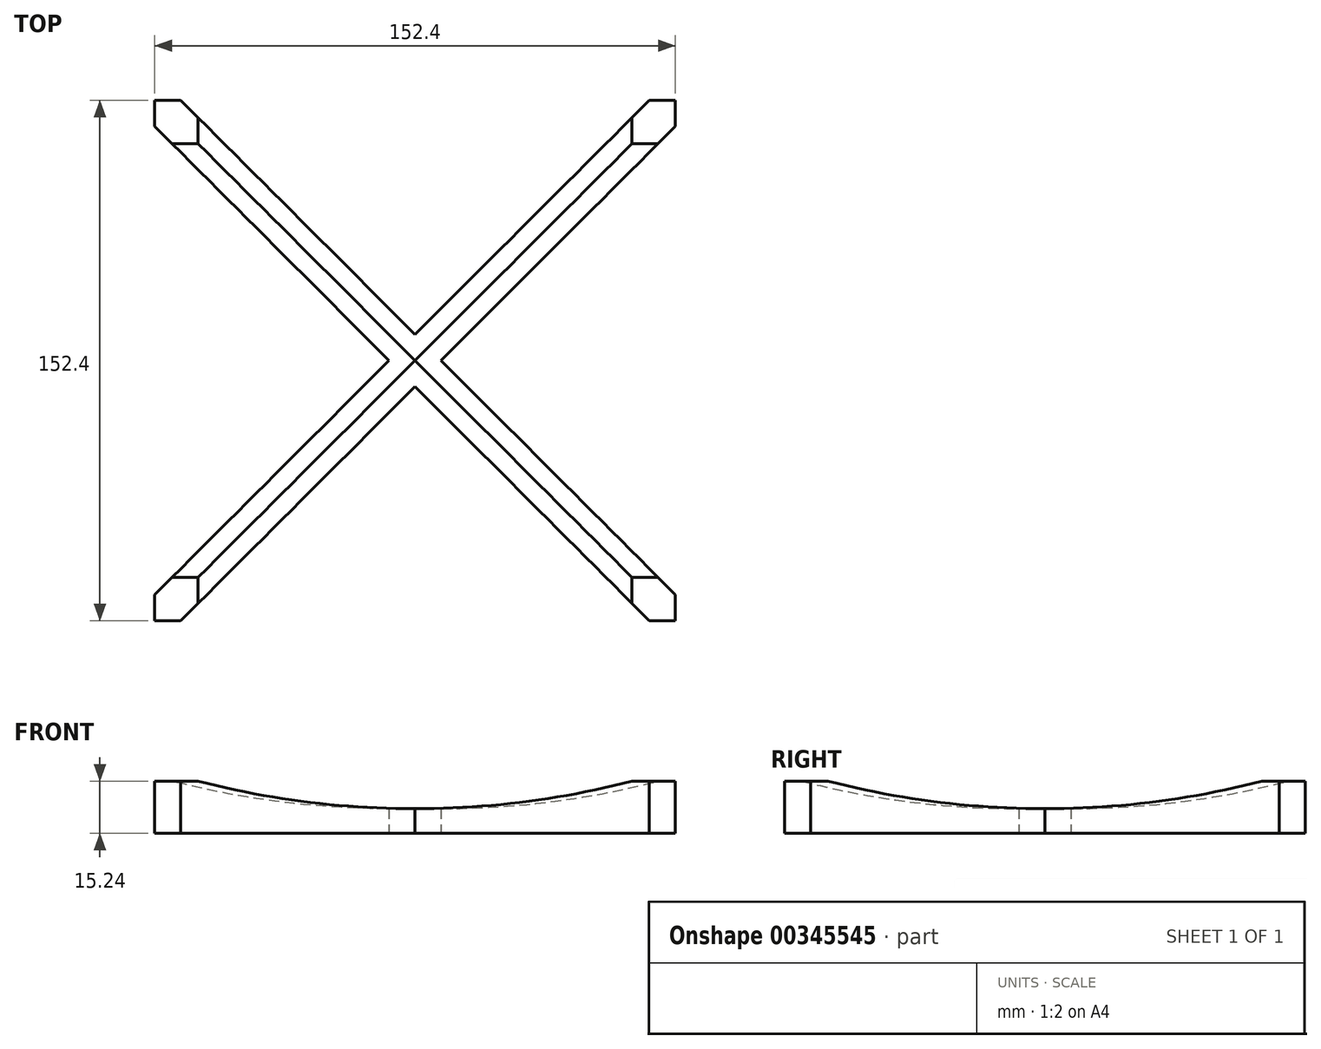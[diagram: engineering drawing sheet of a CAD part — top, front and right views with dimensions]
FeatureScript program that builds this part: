
annotation { "Feature Type Name" : "Feature", "Feature Type Description" : "" }
export const myFeature = defineFeature(function(context is Context, id is Id, definition is map)
    precondition{}
    {
        {
            var Q0;
            Q0=qCreatedBy(makeId("Top.planeOp"),FACE);
            var sketch = newSketch(context, id + "F0", { "sketchPlane" : qUnion([Q0])});
            skLineSegment(sketch, "E0.bottom", {"start": v(-76.16, 76.08) * mm, "end": v(-68.54, 76.08) * mm});
            skLineSegment(sketch, "E0.top", {"start": v(-76.16, -76.32) * mm, "end": v(-68.54, -76.32) * mm});
            skLineSegment(sketch, "E0.left", {"start": v(-76.16, 76.08) * mm, "end": v(-76.16, 68.46) * mm});
            skLineSegment(sketch, "E0.right", {"start": v(76.24, 76.08) * mm, "end": v(76.24, 68.46) * mm});
            skLineSegment(sketch, "E1", {"start": v(-76.16, 68.46) * mm, "end": v(-7.58, -0.12) * mm});
            skLineSegment(sketch, "E2", {"start": v(76.24, -68.7) * mm, "end": v(7.66, -0.12) * mm});
            skLineSegment(sketch, "E3", {"start": v(68.62, 76.08) * mm, "end": v(0.04, 7.5) * mm});
            skLineSegment(sketch, "E4", {"start": v(-68.54, -76.32) * mm, "end": v(0.04, -7.74) * mm});
            skLineSegment(sketch, "E5.trimOffspring", {"start": v(68.62, 76.08) * mm, "end": v(76.24, 76.08) * mm});
            skLineSegment(sketch, "E6.trimOffspring", {"start": v(-76.16, -68.7) * mm, "end": v(-76.16, -76.32) * mm});
            skLineSegment(sketch, "E7.trimOffspring", {"start": v(68.62, -76.32) * mm, "end": v(76.24, -76.32) * mm});
            skLineSegment(sketch, "E8.trimOffspring", {"start": v(76.24, -68.7) * mm, "end": v(76.24, -76.32) * mm});
            skLineSegment(sketch, "E9.trimOffspring", {"start": v(0.04, 7.5) * mm, "end": v(-68.54, 76.08) * mm});
            skLineSegment(sketch, "E10.trimOffspring", {"start": v(-7.58, -0.12) * mm, "end": v(-76.16, -68.7) * mm});
            skLineSegment(sketch, "E11.trimOffspring", {"start": v(0.04, -7.74) * mm, "end": v(68.62, -76.32) * mm});
            skLineSegment(sketch, "E12.trimOffspring", {"start": v(7.66, -0.12) * mm, "end": v(76.24, 68.46) * mm});
            skSolve(sketch);
        }
        {
            var Q0;
            Q0=makeQuery(id+"F0.imprint","IMPRINT",FACE,{"disambiguationData":[TD([[makeQuery(id+"F0.imprint","IMPRINT",EDGE,{"derivedFrom":sQuery(id+"F0.wireOp",EDGE,"E0.bottom")}),-1.0]])]});
            extrude(context, id + "F1", {"entities" : qUnion([Q0]), "depth" : 15.24 * mm});
        }
        {
            var Q0;
            Q0=makeQuery(id+"F1.opExtrude","SWEPT_FACE",FACE,{"disambiguationData":[OSD([sQuery(id+"F0.wireOp",EDGE,"E0.top")])]});
            var sketch = newSketch(context, id + "F2", { "sketchPlane" : qUnion([Q0])});
            skLineSegment(sketch, "E13.bottom", {"start": v(-76.16, 15.24) * mm, "end": v(76.24, 15.24) * mm});
            skLineSegment(sketch, "E13.top", {"start": v(-76.16, 0) * mm, "end": v(76.24, 0) * mm});
            skLineSegment(sketch, "E13.left", {"start": v(-76.16, 15.24) * mm, "end": v(-76.16, 0) * mm});
            skLineSegment(sketch, "E13.right", {"start": v(76.24, 15.24) * mm, "end": v(76.24, 0) * mm});
            skArc(sketch, "E14", {"start": v(-63.46, 15.24) * mm, "mid": v(0.04, 7.17) * mm, "end": v(63.54, 15.24) * mm});
            skSolve(sketch);
        }
        {
            var Q0;
            {var subQ0=sQuery(id+"F2.wireOp",EDGE,"E14");Q0=makeQuery(id+"F2.imprint","IMPRINT",FACE,{"disambiguationData":[TD([[makeQuery(id+"F2.imprint","IMPRINT",EDGE,{"derivedFrom":subQ0}),1.0]])]});}
            extrude(context, id + "F3", {"entities" : qUnion([Q0]), "operationType" : NewBodyOperationType.REMOVE, "endBound" : BoundingType.THROUGH_ALL, "oppositeDirection" : true, "depth" : 25.4 * mm});
        }
        {
            var Q0;
            Q0=makeQuery(id+"F1.opExtrude","SWEPT_FACE",FACE,{"disambiguationData":[OSD([sQuery(id+"F0.wireOp",EDGE,"E0.left")])]});
            var sketch = newSketch(context, id + "F4", { "sketchPlane" : qUnion([Q0])});
            skLineSegment(sketch, "E15.bottom", {"start": v(-76.08, 15.24) * mm, "end": v(76.32, 15.24) * mm});
            skLineSegment(sketch, "E15.top", {"start": v(-76.08, 0) * mm, "end": v(76.32, 0) * mm});
            skLineSegment(sketch, "E15.left", {"start": v(-76.08, 15.24) * mm, "end": v(-76.08, 0) * mm});
            skLineSegment(sketch, "E15.right", {"start": v(76.32, 15.24) * mm, "end": v(76.32, 0) * mm});
            skArc(sketch, "E16", {"start": v(-63.38, 15.24) * mm, "mid": v(0.12, 7.17) * mm, "end": v(63.62, 15.24) * mm});
            skSolve(sketch);
        }
        {
            var Q0;
            {var subQ0=sQuery(id+"F4.wireOp",EDGE,"E16");Q0=makeQuery(id+"F4.imprint","IMPRINT",FACE,{"disambiguationData":[TD([[makeQuery(id+"F4.imprint","IMPRINT",EDGE,{"derivedFrom":subQ0}),1.0]])]});}
            extrude(context, id + "F5", {"entities" : qUnion([Q0]), "operationType" : NewBodyOperationType.REMOVE, "endBound" : BoundingType.THROUGH_ALL, "oppositeDirection" : true, "depth" : 25.4 * mm});
        }
    });
